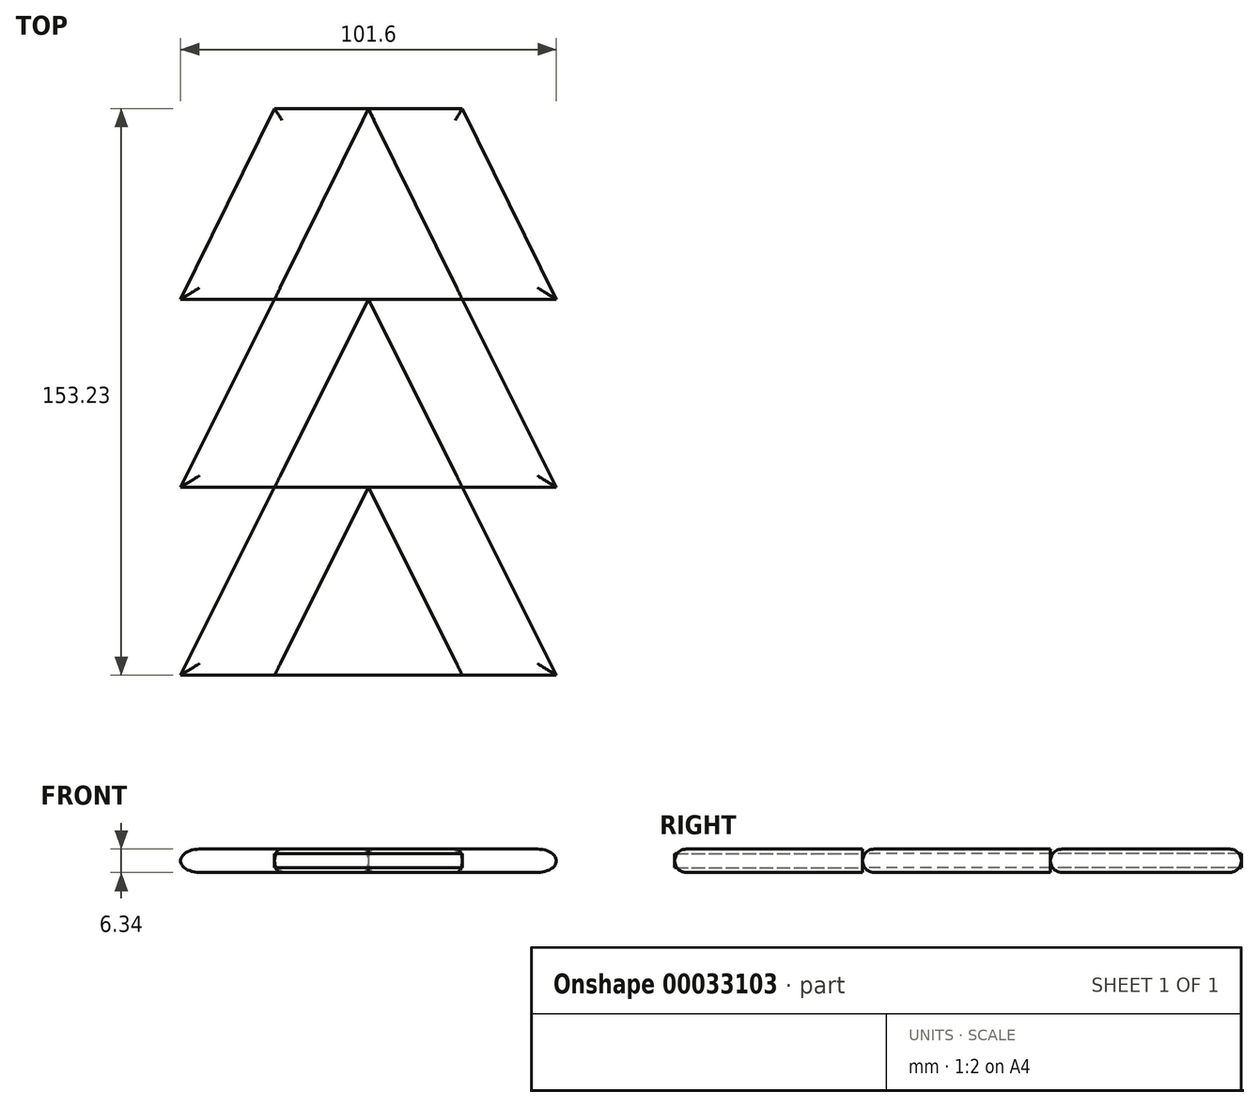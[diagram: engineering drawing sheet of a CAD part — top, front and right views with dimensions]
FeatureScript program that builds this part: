
annotation { "Feature Type Name" : "Feature", "Feature Type Description" : "" }
export const myFeature = defineFeature(function(context is Context, id is Id, definition is map)
    precondition{}
    {
        {
            var Q0;
            Q0=qCreatedBy(makeId("Top.planeOp"),FACE);
            var sketch = newSketch(context, id + "F0", { "sketchPlane" : qUnion([Q0])});
            skLineSegment(sketch, "E0", {"start": v(0, 0) * mm, "end": v(25.4, 0) * mm});
            skLineSegment(sketch, "E1", {"start": v(25.4, 50.8) * mm, "end": v(50.8, 50.8) * mm});
            skLineSegment(sketch, "E2", {"start": v(25.4, 0) * mm, "end": v(50.8, 50.8) * mm});
            skLineSegment(sketch, "E3", {"start": v(25.4, 50.8) * mm, "end": v(0, 0) * mm});
            skLineSegment(sketch, "E4", {"start": v(50.8, 50.8) * mm, "end": v(76.2, 50.8) * mm});
            skLineSegment(sketch, "E5", {"start": v(76.2, 50.8) * mm, "end": v(101.6, 0) * mm});
            skLineSegment(sketch, "E6", {"start": v(101.6, 0) * mm, "end": v(76.2, 0) * mm});
            skLineSegment(sketch, "E7", {"start": v(76.2, 0) * mm, "end": v(50.8, 50.8) * mm});
            skLineSegment(sketch, "E8", {"start": v(25.4, 50.8) * mm, "end": v(0, 50.8) * mm});
            skLineSegment(sketch, "E9", {"start": v(0, 50.8) * mm, "end": v(25.4, 101.6) * mm});
            skLineSegment(sketch, "E10", {"start": v(25.4, 101.6) * mm, "end": v(50.8, 101.6) * mm});
            skLineSegment(sketch, "E11", {"start": v(50.8, 101.6) * mm, "end": v(76.2, 101.6) * mm});
            skLineSegment(sketch, "E12", {"start": v(76.2, 101.6) * mm, "end": v(101.6, 50.8) * mm});
            skLineSegment(sketch, "E13", {"start": v(76.2, 50.8) * mm, "end": v(101.6, 50.8) * mm});
            skLineSegment(sketch, "E14", {"start": v(50.8, 101.6) * mm, "end": v(76.2, 50.8) * mm});
            skLineSegment(sketch, "E15", {"start": v(50.8, 101.6) * mm, "end": v(25.4, 50.8) * mm});
            skLineSegment(sketch, "E16", {"start": v(25.4, 101.6) * mm, "end": v(0, 101.6) * mm});
            skLineSegment(sketch, "E17", {"start": v(0, 101.6) * mm, "end": v(25.4, 153.23) * mm});
            skLineSegment(sketch, "E18", {"start": v(25.4, 153.23) * mm, "end": v(50.8, 153.23) * mm});
            skLineSegment(sketch, "E19", {"start": v(50.8, 153.23) * mm, "end": v(25.4, 101.6) * mm});
            skLineSegment(sketch, "E20", {"start": v(76.2, 101.6) * mm, "end": v(101.6, 101.6) * mm});
            skLineSegment(sketch, "E21", {"start": v(101.6, 101.6) * mm, "end": v(76.2, 153.23) * mm});
            skLineSegment(sketch, "E22", {"start": v(76.2, 153.23) * mm, "end": v(50.8, 153.23) * mm});
            skLineSegment(sketch, "E23", {"start": v(50.8, 153.23) * mm, "end": v(76.2, 101.6) * mm});
            skLineSegment(sketch, "E24", {"start": v(25.4, 0) * mm, "end": v(76.2, 0) * mm});
            skSolve(sketch);
        }
        {
            var Q0;
            Q0=makeQuery(id+"F0.imprint","IMPRINT",FACE,{"disambiguationData":[TD([[makeQuery(id+"F0.imprint","IMPRINT",EDGE,{"derivedFrom":sQuery(id+"F0.wireOp",EDGE,"E16")}),-1.0]])]});
            var Q1;
            Q1=makeQuery(id+"F0.imprint","IMPRINT",FACE,{"disambiguationData":[TD([[makeQuery(id+"F0.imprint","IMPRINT",EDGE,{"derivedFrom":sQuery(id+"F0.wireOp",EDGE,"E20")}),1.0]])]});
            var Q2;
            Q2=makeQuery(id+"F0.imprint","IMPRINT",FACE,{"disambiguationData":[TD([[makeQuery(id+"F0.imprint","IMPRINT",EDGE,{"derivedFrom":sQuery(id+"F0.wireOp",EDGE,"E11")}),-1.0]])]});
            var Q3;
            Q3=makeQuery(id+"F0.imprint","IMPRINT",FACE,{"disambiguationData":[TD([[makeQuery(id+"F0.imprint","IMPRINT",EDGE,{"derivedFrom":sQuery(id+"F0.wireOp",EDGE,"E8")}),-1.0]])]});
            var Q4;
            Q4=makeQuery(id+"F0.imprint","IMPRINT",FACE,{"disambiguationData":[TD([[makeQuery(id+"F0.imprint","IMPRINT",EDGE,{"derivedFrom":sQuery(id+"F0.wireOp",EDGE,"E0")}),1.0]])]});
            var Q5;
            Q5=makeQuery(id+"F0.imprint","IMPRINT",FACE,{"disambiguationData":[TD([[makeQuery(id+"F0.imprint","IMPRINT",EDGE,{"derivedFrom":sQuery(id+"F0.wireOp",EDGE,"E4")}),-1.0]])]});
            extrude(context, id + "F1", {"entities" : qUnion([Q0, Q1, Q2, Q3, Q4, Q5]), "endBound" : BoundingType.SYMMETRIC, "depth" : 6.35 * mm});
        }
        {
            var Q0;
            Q0=makeQuery(id+"F0.imprint","IMPRINT",FACE,{"disambiguationData":[TD([[makeQuery(id+"F0.imprint","IMPRINT",EDGE,{"derivedFrom":sQuery(id+"F0.wireOp",EDGE,"E10")}),1.0]])]});
            var Q1;
            Q1=makeQuery(id+"F0.imprint","IMPRINT",FACE,{"disambiguationData":[TD([[makeQuery(id+"F0.imprint","IMPRINT",EDGE,{"derivedFrom":sQuery(id+"F0.wireOp",EDGE,"E1")}),1.0]])]});
            var Q2;
            Q2=makeQuery(id+"F0.imprint","IMPRINT",FACE,{"disambiguationData":[TD([[makeQuery(id+"F0.imprint","IMPRINT",EDGE,{"derivedFrom":sQuery(id+"F0.wireOp",EDGE,"E2")}),-1.0]])]});
            extrude(context, id + "F2", {"entities" : qUnion([Q0, Q1, Q2]), "endBound" : BoundingType.SYMMETRIC, "depth" : 3.8 * mm});
        }
        {
            var Q0;
            Q0=makeQuery(id+"F1.opExtrude","CAP_EDGE",EDGE,{"disambiguationData":[OSD([sQuery(id+"F0.wireOp",EDGE,"E3")])],"isStart":false});
            var Q1;
            Q1=makeQuery(id+"F1.opExtrude","CAP_EDGE",EDGE,{"disambiguationData":[OSD([sQuery(id+"F0.wireOp",EDGE,"E9")])],"isStart":false});
            var Q2;
            Q2=makeQuery(id+"F1.opExtrude","CAP_EDGE",EDGE,{"disambiguationData":[OSD([sQuery(id+"F0.wireOp",EDGE,"E17")])],"isStart":false});
            var Q3;
            Q3=makeQuery(id+"F1.opExtrude","CAP_EDGE",EDGE,{"disambiguationData":[OSD([sQuery(id+"F0.wireOp",EDGE,"E21")])],"isStart":false});
            var Q4;
            Q4=makeQuery(id+"F1.opExtrude","CAP_EDGE",EDGE,{"disambiguationData":[OSD([sQuery(id+"F0.wireOp",EDGE,"E12")])],"isStart":false});
            var Q5;
            Q5=makeQuery(id+"F1.opExtrude","CAP_EDGE",EDGE,{"disambiguationData":[OSD([sQuery(id+"F0.wireOp",EDGE,"E5")])],"isStart":false});
            var Q6;
            Q6=makeQuery(id+"F1.opExtrude","CAP_EDGE",EDGE,{"disambiguationData":[OSD([sQuery(id+"F0.wireOp",EDGE,"E17")])],"isStart":true});
            var Q7;
            Q7=makeQuery(id+"F1.opExtrude","CAP_EDGE",EDGE,{"disambiguationData":[OSD([sQuery(id+"F0.wireOp",EDGE,"E21")])],"isStart":true});
            var Q8;
            Q8=makeQuery(id+"F1.opExtrude","CAP_EDGE",EDGE,{"disambiguationData":[OSD([sQuery(id+"F0.wireOp",EDGE,"E12")])],"isStart":true});
            var Q9;
            Q9=makeQuery(id+"F1.opExtrude","CAP_EDGE",EDGE,{"disambiguationData":[OSD([sQuery(id+"F0.wireOp",EDGE,"E5")])],"isStart":true});
            var Q10;
            Q10=makeQuery(id+"F1.opExtrude","CAP_EDGE",EDGE,{"disambiguationData":[OSD([sQuery(id+"F0.wireOp",EDGE,"E3")])],"isStart":true});
            var Q11;
            Q11=makeQuery(id+"F1.opExtrude","CAP_EDGE",EDGE,{"disambiguationData":[OSD([sQuery(id+"F0.wireOp",EDGE,"E9")])],"isStart":true});
            var Q12;
            Q12=makeQuery(id+"F1.opExtrude","CAP_EDGE",EDGE,{"disambiguationData":[OSD([sQuery(id+"F0.wireOp",EDGE,"E18")])],"isStart":true});
            var Q13;
            Q13=makeQuery(id+"F1.opExtrude","CAP_EDGE",EDGE,{"disambiguationData":[OSD([sQuery(id+"F0.wireOp",EDGE,"E18")])],"isStart":false});
            var Q14;
            Q14=makeQuery(id+"F1.opExtrude","CAP_EDGE",EDGE,{"disambiguationData":[OSD([sQuery(id+"F0.wireOp",EDGE,"E22")])],"isStart":false});
            var Q15;
            Q15=makeQuery(id+"F1.opExtrude","CAP_EDGE",EDGE,{"disambiguationData":[OSD([sQuery(id+"F0.wireOp",EDGE,"E22")])],"isStart":true});
            var Q16;
            Q16=makeQuery(id+"F1.opExtrude","CAP_EDGE",EDGE,{"disambiguationData":[OSD([sQuery(id+"F0.wireOp",EDGE,"E20")])],"isStart":false});
            var Q17;
            Q17=makeQuery(id+"F1.opExtrude","CAP_EDGE",EDGE,{"disambiguationData":[OSD([sQuery(id+"F0.wireOp",EDGE,"E16")])],"isStart":false});
            var Q18;
            Q18=makeQuery(id+"F1.opExtrude","CAP_EDGE",EDGE,{"disambiguationData":[OSD([sQuery(id+"F0.wireOp",EDGE,"E16")])],"isStart":true});
            var Q19;
            Q19=makeQuery(id+"F1.opExtrude","CAP_EDGE",EDGE,{"disambiguationData":[OSD([sQuery(id+"F0.wireOp",EDGE,"E20")])],"isStart":true});
            var Q20;
            Q20=makeQuery(id+"F1.opExtrude","CAP_EDGE",EDGE,{"disambiguationData":[OSD([sQuery(id+"F0.wireOp",EDGE,"E13")])],"isStart":true});
            var Q21;
            Q21=makeQuery(id+"F1.opExtrude","CAP_EDGE",EDGE,{"disambiguationData":[OSD([sQuery(id+"F0.wireOp",EDGE,"E13")])],"isStart":false});
            var Q22;
            Q22=makeQuery(id+"F1.opExtrude","CAP_EDGE",EDGE,{"disambiguationData":[OSD([sQuery(id+"F0.wireOp",EDGE,"E8")])],"isStart":false});
            var Q23;
            Q23=makeQuery(id+"F1.opExtrude","CAP_EDGE",EDGE,{"disambiguationData":[OSD([sQuery(id+"F0.wireOp",EDGE,"E8")])],"isStart":true});
            var Q24;
            Q24=makeQuery(id+"F1.opExtrude","CAP_EDGE",EDGE,{"disambiguationData":[OSD([sQuery(id+"F0.wireOp",EDGE,"E0")])],"isStart":false});
            var Q25;
            Q25=makeQuery(id+"F1.opExtrude","CAP_EDGE",EDGE,{"disambiguationData":[OSD([sQuery(id+"F0.wireOp",EDGE,"E0")])],"isStart":true});
            var Q26;
            Q26=makeQuery(id+"F1.opExtrude","CAP_EDGE",EDGE,{"disambiguationData":[OSD([sQuery(id+"F0.wireOp",EDGE,"E6")])],"isStart":false});
            var Q27;
            Q27=makeQuery(id+"F1.opExtrude","CAP_EDGE",EDGE,{"disambiguationData":[OSD([sQuery(id+"F0.wireOp",EDGE,"E6")])],"isStart":true});
            fillet(context, id + "F3", {"entities" : qUnion([Q0, Q1, Q2, Q3, Q4, Q5, Q6, Q7, Q8, Q9, Q10, Q11, Q12, Q13, Q14, Q15, Q16, Q17, Q18, Q19, Q20, Q21, Q22, Q23, Q24, Q25, Q26, Q27]), "radius" : 3.17 * mm, "tangentPropagation" : true, "allowEdgeOverflow" : false});
        }
    });
